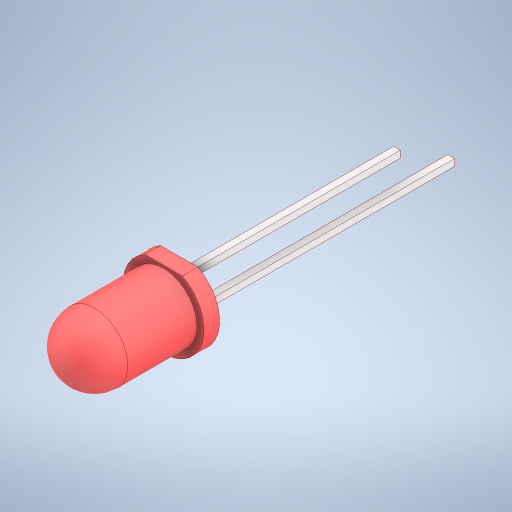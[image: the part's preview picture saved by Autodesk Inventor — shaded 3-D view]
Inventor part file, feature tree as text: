
AUTODESK INVENTOR PART (.ipt)
format: ipt  version: 2023 (Build 270158000, 158)  size: 277,504 bytes
history: mixed  units: in
note: dims shown in document units (in); Inventor stores cm internally (conversion verified against a paired STEP export)
features: extrude x1, imported_body x1
ambient origin geometry x8: Origin, YZ Plane, XZ Plane, XY Plane, X Axis, Y Axis, Z Axis, Center Point
bodies: Solid1 (imported_parasolid)
feature tree (2):
  extrude  "Extrude5"  [1 undecoded]
  imported_body  NMx_Import_Brep_tag  [imported B-rep: ~16 faces, bbox_mm=[4.94, 4.15, 26.23]]
note: 1 required parameter value undecoded (feature->parameter linkage not recoverable at this tier; creation-order binding heuristic only, values carry confidence <= 0.55)
